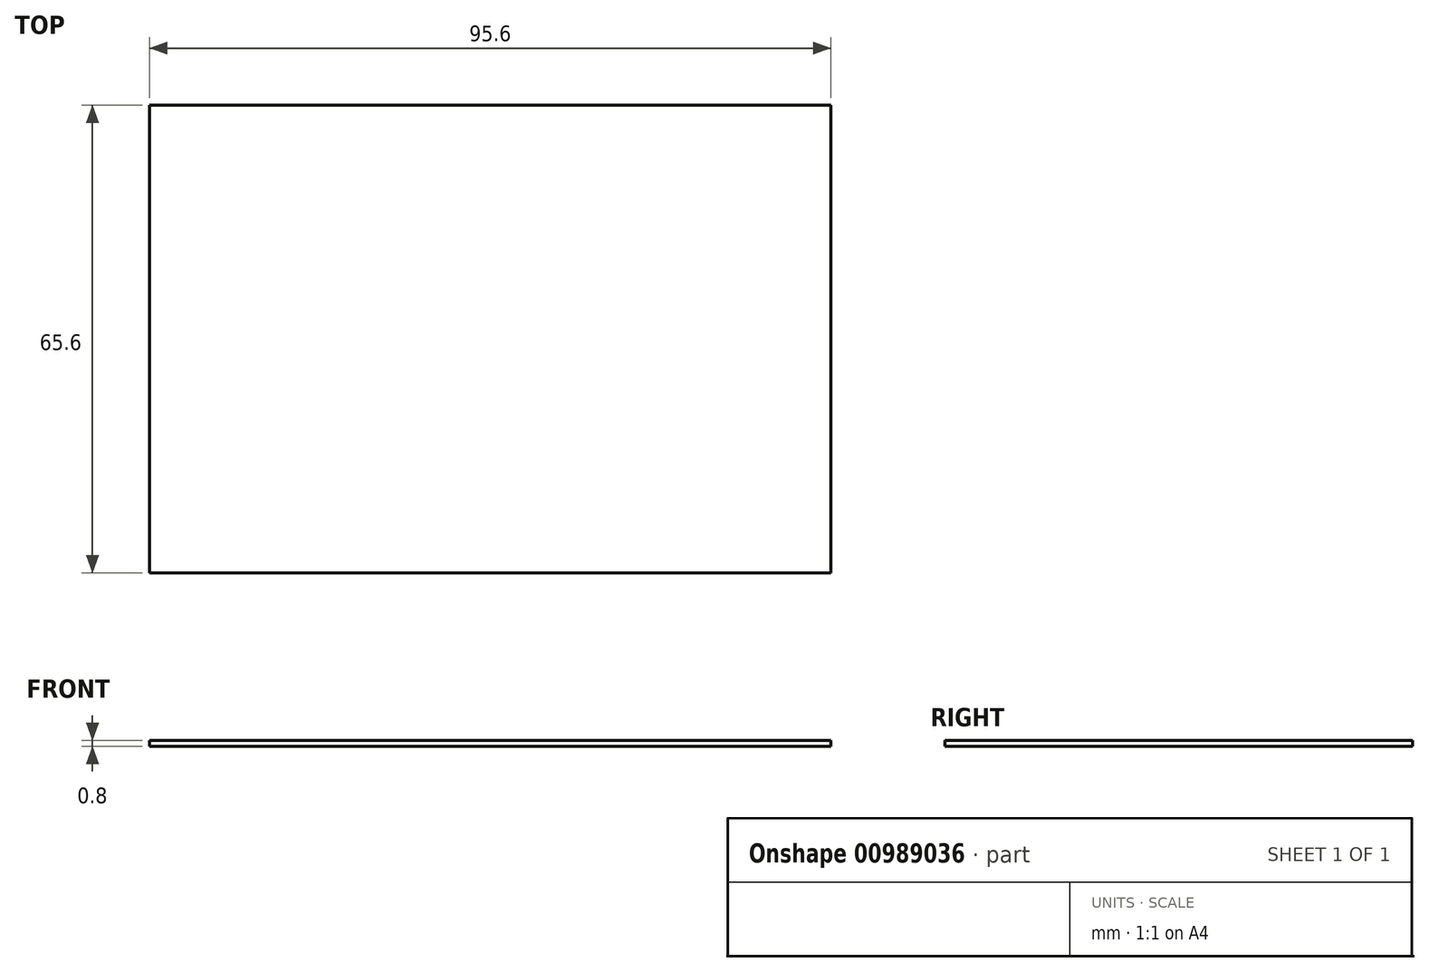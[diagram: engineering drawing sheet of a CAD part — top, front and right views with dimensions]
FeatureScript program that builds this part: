
annotation { "Feature Type Name" : "Feature", "Feature Type Description" : "" }
export const myFeature = defineFeature(function(context is Context, id is Id, definition is map)
    precondition{}
    {
        {
            var Q0;
            Q0=qCreatedBy(makeId("Top.planeOp"),FACE);
            var sketch = newSketch(context, id + "F0", { "sketchPlane" : qUnion([Q0])});
            skLineSegment(sketch, "E0.bottom", {"start": v(47.8, -32.8) * mm, "end": v(-47.8, -32.8) * mm});
            skLineSegment(sketch, "E0.top", {"start": v(47.8, 32.8) * mm, "end": v(-47.8, 32.8) * mm});
            skLineSegment(sketch, "E0.left", {"start": v(47.8, -32.8) * mm, "end": v(47.8, 32.8) * mm});
            skLineSegment(sketch, "E0.right", {"start": v(-47.8, -32.8) * mm, "end": v(-47.8, 32.8) * mm});
            skPoint(sketch, "E0.middle", {"position": v(0, 0) * mm});
            skSolve(sketch);
        }
        {
            var Q0;
            Q0=makeQuery(id+"F0.imprint","IMPRINT",FACE,{"disambiguationData":[TD([[makeQuery(id+"F0.imprint","IMPRINT",EDGE,{"derivedFrom":sQuery(id+"F0.wireOp",EDGE,"E0.bottom")}),-1.0]])]});
            extrude(context, id + "F1", {"entities" : qUnion([Q0]), "depth" : 0.8 * mm, "offsetDistance" : 25 * mm});
        }
    });
